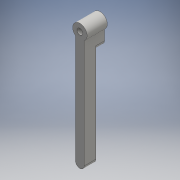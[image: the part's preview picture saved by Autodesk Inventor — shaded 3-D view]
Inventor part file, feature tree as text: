
AUTODESK INVENTOR PART (.ipt)
format: ipt  version: 2016 (Build 200138000, 138)  size: 126,464 bytes
history: native  units: mm
features: extrude x2, sketch x2, other x1, fillet x1, projected_geometry x1
ambient origin geometry x8: Origin, YZ Plane, XZ Plane, XY Plane, X Axis, Y Axis, Z Axis, Center Point
bodies: Solid1 (feature_tree)
feature tree (7):
  other  "<userpath>\Documents\GitHub\3D\Hoja Oculta\Parametros.xlsx"
  extrude  "Base"  Depth=3.0mm
  extrude  "Superior"  Depth=1.5mm
  fillet  "Biselado"  Radius=4.0mm
  sketch  "Sketch1"  dims[d0=39.0mm d1=3.0mm]
  sketch  "Sketch2"  dims[d2=5.0mm d3=2.0mm d4=4.0mm d5=0.0mm d8=5.0mm d9=3.0mm d10=0.0mm d11=1.5mm]
  projected_geometry  "Projected Loop1"
